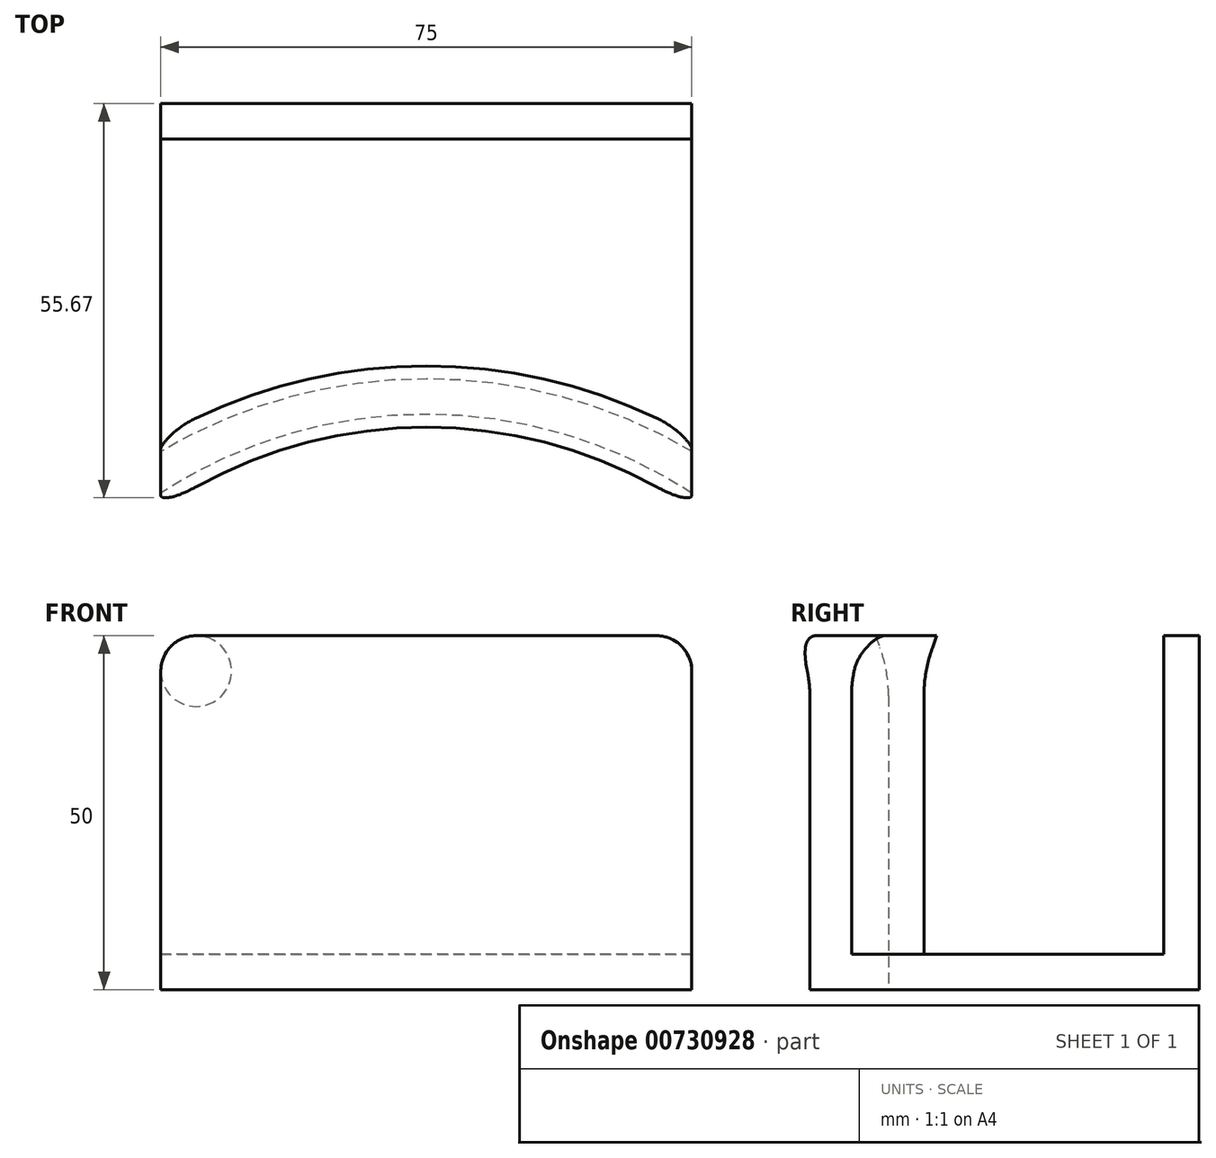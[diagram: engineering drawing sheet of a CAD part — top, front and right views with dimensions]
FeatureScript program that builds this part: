
annotation { "Feature Type Name" : "Feature", "Feature Type Description" : "" }
export const myFeature = defineFeature(function(context is Context, id is Id, definition is map)
    precondition{}
    {
        {
            var Q0;
            Q0=qCreatedBy(makeId("Top.planeOp"),FACE);
            var sketch = newSketch(context, id + "F0", { "sketchPlane" : qUnion([Q0])});
            skLineSegment(sketch, "E0.bottom", {"start": v(38.22, 38) * mm, "end": v(-36.78, 38) * mm});
            skLineSegment(sketch, "E0.left", {"start": v(38.22, 38) * mm, "end": v(38.22, -17) * mm});
            skLineSegment(sketch, "E0.right", {"start": v(-36.78, 38) * mm, "end": v(-36.78, -17) * mm});
            skPoint(sketch, "E0.middle", {"position": v(0, 0) * mm});
            skLineSegment(sketch, "E1", {"start": v(-36.78, 33) * mm, "end": v(38.22, 33) * mm});
            skArc(sketch, "E2", {"start": v(38.22, -17) * mm, "mid": v(0.72, -5.89) * mm, "end": v(-36.78, -17) * mm});
            skArc(sketch, "E3.0", {"start": v(38.22, -11.12) * mm, "mid": v(0.72, -0.89) * mm, "end": v(-36.78, -11.12) * mm});
            skLineSegment(sketch, "E4", {"start": v(-44.66, -17) * mm, "end": v(48.17, -17) * mm, "construction": true});
            skSolve(sketch);
        }
        {
            var Q0;
            {var subQ0=sQuery(id+"F0.wireOp",EDGE,"E0.bottom");Q0=makeQuery(id+"F0.imprint","IMPRINT",FACE,{"disambiguationData":[TD([[makeQuery(id+"F0.imprint","IMPRINT",EDGE,{"derivedFrom":subQ0}),1.0]])]});}
            extrude(context, id + "F1", {"entities" : qUnion([Q0]), "depth" : 50 * mm, "offsetDistance" : 25 * mm});
        }
        {
            var Q0;
            {var subQ0=sQuery(id+"F0.wireOp",EDGE,"E1");Q0=makeQuery(id+"F0.imprint","IMPRINT",FACE,{"disambiguationData":[TD([[makeQuery(id+"F0.imprint","IMPRINT",EDGE,{"derivedFrom":subQ0}),-1.0]])]});}
            extrude(context, id + "F2", {"entities" : qUnion([Q0]), "operationType" : NewBodyOperationType.ADD, "depth" : 5 * mm, "offsetDistance" : 25 * mm});
        }
        {
            var Q0;
            {var subQ0=sQuery(id+"F0.wireOp",EDGE,"E2");Q0=makeQuery(id+"F0.imprint","IMPRINT",FACE,{"disambiguationData":[TD([[makeQuery(id+"F0.imprint","IMPRINT",EDGE,{"derivedFrom":subQ0}),-1.0]])]});}
            extrude(context, id + "F3", {"entities" : qUnion([Q0]), "operationType" : NewBodyOperationType.ADD, "depth" : 45 * mm, "offsetDistance" : 25 * mm});
        }
        {
            var Q0;
            Q0=makeQuery(id+"F3.opExtrude","CAP_FACE",FACE,{"disambiguationData":[OSD([sQuery(id+"F0.wireOp",EDGE,"E0.left"),sQuery(id+"F0.wireOp",EDGE,"E0.right"),sQuery(id+"F0.wireOp",EDGE,"E2"),sQuery(id+"F0.wireOp",EDGE,"E3.0")])],"isStart":false});
            extrude(context, id + "F4", {"entities" : qUnion([Q0]), "operationType" : NewBodyOperationType.ADD, "depth" : 5 * mm, "offsetDistance" : 25 * mm, "hasDraft" : true, "draftAngle" : 20 * degree});
        }
        {
            var Q0;
            Q0=makeQuery(id+"F1.opExtrude","CAP_EDGE",EDGE,{"disambiguationData":[OSD([sQuery(id+"F0.wireOp",EDGE,"E0.right")])],"isStart":false});
            var Q1;
            Q1=makeQuery(id+"F1.opExtrude","CAP_EDGE",EDGE,{"disambiguationData":[OSD([sQuery(id+"F0.wireOp",EDGE,"E0.left")])],"isStart":false});
            var Q2;
            Q2=makeQuery(id+"F4.opExtrude","CAP_EDGE",EDGE,{"disambiguationData":[OSD([sQuery(id+"F0.wireOp",EDGE,"E0.right")])],"isStart":false});
            var Q3;
            Q3=makeQuery(id+"F4.opExtrude","CAP_EDGE",EDGE,{"disambiguationData":[OSD([sQuery(id+"F0.wireOp",EDGE,"E0.left")])],"isStart":false});
            var Q4;
            Q4=makeQuery(id+"F2.opExtrude","CAP_EDGE",EDGE,{"disambiguationData":[OSD([sQuery(id+"F0.wireOp",EDGE,"E1")])],"isStart":false});
            var Q5;
            Q5=makeQuery(id+"F2.opExtrude","CAP_EDGE",EDGE,{"disambiguationData":[OSD([sQuery(id+"F0.wireOp",EDGE,"E3.0")])],"isStart":false});
            fillet(context, id + "F5", {"entities" : qUnion([Q0, Q1, Q2, Q3, Q4, Q5]), "radius" : 5 * mm, "tangentPropagation" : true, "allowEdgeOverflow" : false});
        }
        {
            var Q0;
            {var subQ0=sQuery(id+"F0.wireOp",EDGE,"E3.0");Q0=makeQuery(id+"F4.boolean.opBoolean","MERGE",EDGE,{"derivedFrom":[makeQuery(id+"F3.opExtrude","CAP_EDGE",EDGE,{"disambiguationData":[OSD([subQ0])],"isStart":false}),makeQuery(id+"F4.opExtrude","CAP_EDGE",EDGE,{"disambiguationData":[OSD([subQ0])],"isStart":true})]});}
            var Q1;
            {var subQ0=sQuery(id+"F0.wireOp",EDGE,"E2");Q1=makeQuery(id+"F4.boolean.opBoolean","MERGE",EDGE,{"derivedFrom":[makeQuery(id+"F3.opExtrude","CAP_EDGE",EDGE,{"disambiguationData":[OSD([subQ0])],"isStart":false}),makeQuery(id+"F4.opExtrude","CAP_EDGE",EDGE,{"disambiguationData":[OSD([subQ0])],"isStart":true})]});}
            fillet(context, id + "F6", {"entities" : qUnion([Q0, Q1]), "radius" : 20 * mm, "tangentPropagation" : true, "allowEdgeOverflow" : false});
        }
    });
